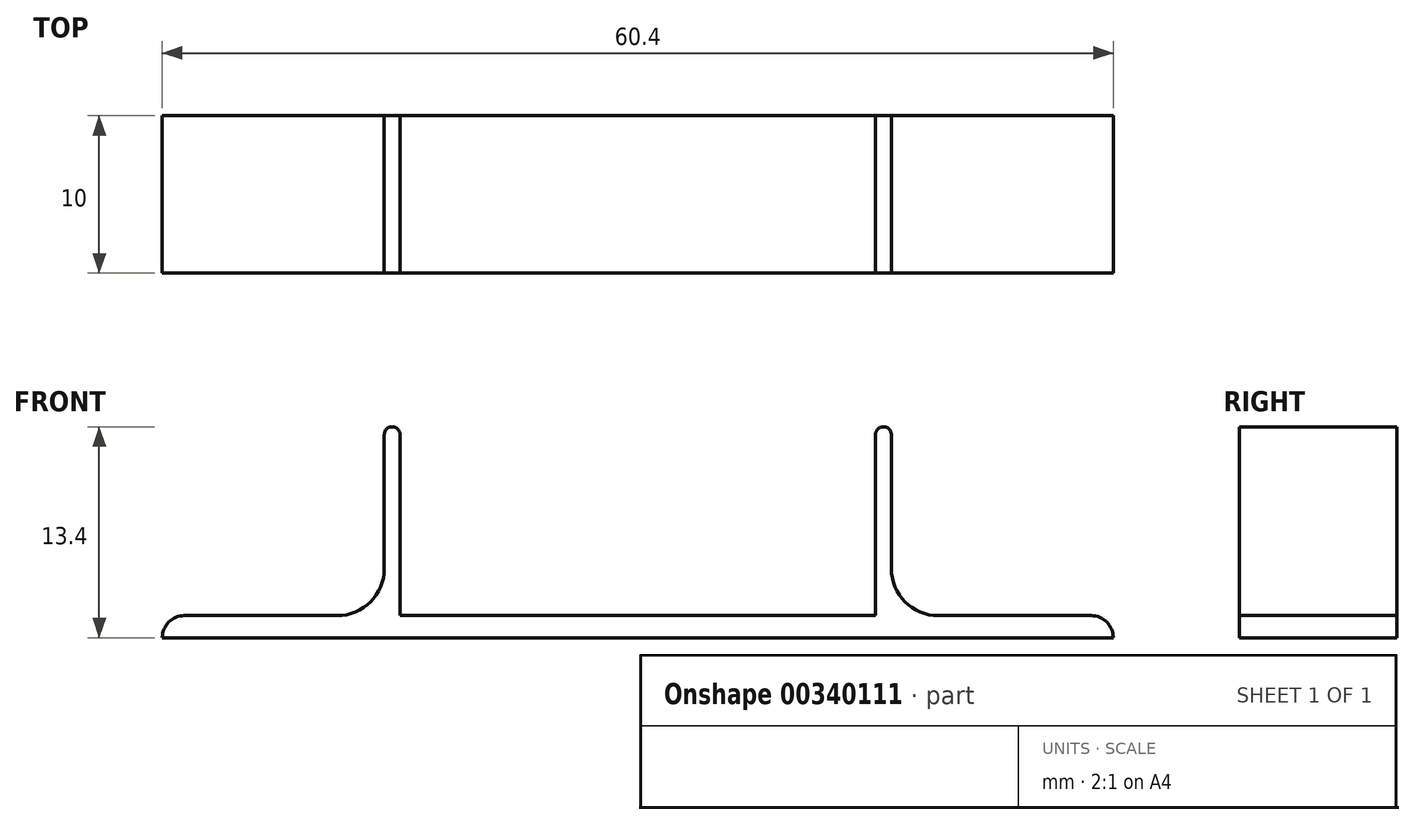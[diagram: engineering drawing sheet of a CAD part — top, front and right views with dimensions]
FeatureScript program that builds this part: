
annotation { "Feature Type Name" : "Feature", "Feature Type Description" : "" }
export const myFeature = defineFeature(function(context is Context, id is Id, definition is map)
    precondition{}
    {
        {
            var Q0;
            Q0=qCreatedBy(makeId("Front.planeOp"),FACE);
            var sketch = newSketch(context, id + "F0", { "sketchPlane" : qUnion([Q0])});
            skLineSegment(sketch, "E0.bottom", {"start": v(0, 0) * mm, "end": v(-30.2, 0) * mm});
            skLineSegment(sketch, "E0.top", {"start": v(0, 1.4) * mm, "end": v(-15.1, 1.4) * mm});
            skLineSegment(sketch, "E0.left", {"start": v(0, 0) * mm, "end": v(0, 1.4) * mm});
            skLineSegment(sketch, "E0.right", {"start": v(-30.2, 0) * mm, "end": v(-30.2, 0) * mm});
            skLineSegment(sketch, "E1.top", {"start": v(-15.6, 13.4) * mm, "end": v(-15.6, 13.4) * mm});
            skLineSegment(sketch, "E1.left", {"start": v(-16.1, 4.4) * mm, "end": v(-16.1, 12.9) * mm});
            skLineSegment(sketch, "E1.right", {"start": v(-15.1, 1.4) * mm, "end": v(-15.1, 12.9) * mm});
            skLineSegment(sketch, "E2", {"start": v(-19.1, 1.4) * mm, "end": v(-28.8, 1.4) * mm});
            skArc(sketch, "E3.filletArc", {"start": v(-19.1, 1.4) * mm, "mid": v(-16.98, 2.28) * mm, "end": v(-16.1, 4.4) * mm});
            skPoint(sketch, "E4.visualSharp", {"position": v(-30.2, 1.4) * mm});
            skArc(sketch, "E4.filletArc", {"start": v(-28.8, 1.4) * mm, "mid": v(-29.79, 0.99) * mm, "end": v(-30.2, 0) * mm});
            skPoint(sketch, "E5.visualSharp", {"position": v(-15.1, 13.4) * mm});
            skArc(sketch, "E5.filletArc", {"start": v(-15.1, 12.9) * mm, "mid": v(-15.25, 13.25) * mm, "end": v(-15.6, 13.4) * mm});
            skPoint(sketch, "E6.visualSharp", {"position": v(-16.1, 13.4) * mm});
            skArc(sketch, "E6.filletArc", {"start": v(-15.6, 13.4) * mm, "mid": v(-15.95, 13.25) * mm, "end": v(-16.1, 12.9) * mm});
            skArc(sketch, "E7.MirrorCS", {"start": v(15.1, 12.9) * mm, "mid": v(15.25, 13.25) * mm, "end": v(15.6, 13.4) * mm});
            skArc(sketch, "E8.MirrorCS", {"start": v(15.6, 13.4) * mm, "mid": v(15.95, 13.25) * mm, "end": v(16.1, 12.9) * mm});
            skArc(sketch, "E9.MirrorCS", {"start": v(28.8, 1.4) * mm, "mid": v(29.79, 0.99) * mm, "end": v(30.2, 0) * mm});
            skPoint(sketch, "E10.MirrorP", {"position": v(15.1, 13.4) * mm});
            skLineSegment(sketch, "E11.MirrorCS", {"start": v(0, 0) * mm, "end": v(30.2, 0) * mm});
            skLineSegment(sketch, "E12.MirrorCS", {"start": v(19.1, 1.4) * mm, "end": v(28.8, 1.4) * mm});
            skLineSegment(sketch, "E13.MirrorCS", {"start": v(15.1, 1.4) * mm, "end": v(15.1, 12.9) * mm});
            skLineSegment(sketch, "E14.MirrorCS", {"start": v(16.1, 4.4) * mm, "end": v(16.1, 12.9) * mm});
            skLineSegment(sketch, "E15.MirrorCS", {"start": v(0, 1.4) * mm, "end": v(15.1, 1.4) * mm});
            skPoint(sketch, "E16.MirrorP", {"position": v(30.2, 1.4) * mm});
            skPoint(sketch, "E17.MirrorP", {"position": v(16.1, 13.4) * mm});
            skArc(sketch, "E18.MirrorCS", {"start": v(19.1, 1.4) * mm, "mid": v(16.98, 2.28) * mm, "end": v(16.1, 4.4) * mm});
            skSolve(sketch);
        }
        {
            var Q0;
            Q0 = qSketchRegion(id + "F0", true);
            extrude(context, id + "F1", {"entities" : qUnion([Q0]), "depth" : 10 * mm});
        }
    });
